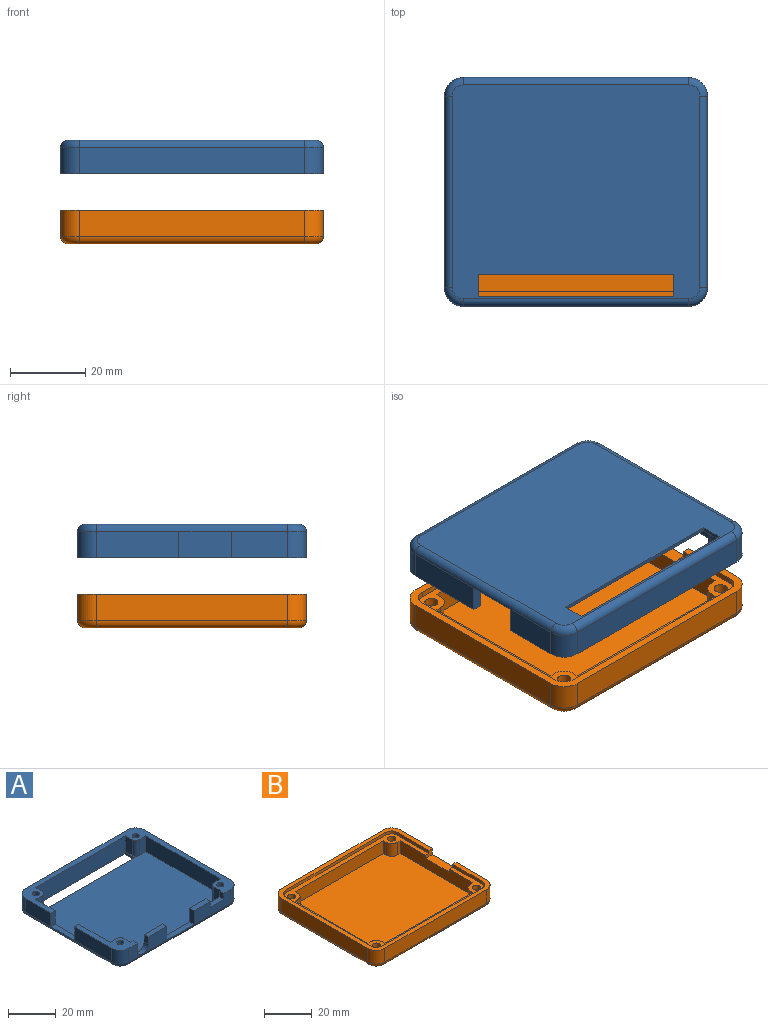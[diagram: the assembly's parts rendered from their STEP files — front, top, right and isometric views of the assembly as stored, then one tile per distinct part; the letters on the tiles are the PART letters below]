
ASSEMBLY  parts=2 mates=1
PART A: 64 faces, bbox 70.8x61.8x9 mm
  f0: plane 15x7mm, normal (-1,0,0), area 105mm2, adj f3,f29,f38,f49
  f1: plane 8.25x7mm, normal (0,-1,0), area 37.3mm2, adj f8,f30,f36,f45,f63
  f2: plane 14.25x7mm, normal (0,-1,0), area 79.3mm2, adj f6,f33,f37,f45,f63
  f3: plane 70x61mm, normal (0,0,1), area 449.4mm2, adj f0,f4,f7,f9,f11,f12,f14,f15
  f4: plane 53x8mm, normal (0,1,0), area 247mm2, adj f3,f5,f6,f8,f21,f22,f24,f33
  f5: plane 9.5x2.5mm, normal (0,0,1), area 23.7mm2, adj f4,f11,f34,f41
  f6: plane 11x2.5mm, normal (0,0,1), area 27.5mm2, adj f2,f4,f33,f37
  f7: plane 44x8mm, normal (1,0,0), area 254mm2, adj f3,f8,f14,f23,f24,f38,f39,f40
  f8: plane 27x10mm, normal (0,0,1), area 109mm2, adj f1,f4,f7,f10,f22,f23,f28,f30
  f9: plane 60x7mm, normal (0,1,0), area 420mm2, adj f3,f29,f32,f50
  f10: plane 22x7mm, normal (-1,0,0), area 154mm2, adj f8,f30,f39,f49
  f11: plane 21.5x7mm, normal (0,-1,0), area 126.5mm2, adj f3,f5,f31,f34,f41,f42,f43,f45
  f12: plane 51x7mm, normal (1,0,0), area 357mm2, adj f3,f31,f32,f46
  f13: plane 66x57mm, normal (0,0,-1), area 3442.3mm2, adj f16,f44,f45,f46,f47,f48,f49,f50
  f14: plane 8x4mm, normal (0,-1,0), area 32mm2, adj f3,f7,f24,f25
  f15: plane 8x4mm, normal (1,0,0), area 32mm2, adj f3,f16,f24,f25
  f16: plane 53x9mm, normal (0,-1,0), area 476mm2, adj f3,f13,f15,f17,f24,f52,f54
  f17: plane 8x4mm, normal (-1,0,0), area 32mm2, adj f3,f16,f24,f26
  f18: plane 8x4mm, normal (0,-1,0), area 32mm2, adj f3,f19,f24,f26
  f19: plane 44x8mm, normal (-1,0,0), area 352mm2, adj f3,f18,f20,f24
  f20: plane 8x4mm, normal (0,1,0), area 32mm2, adj f3,f19,f24,f27
  f21: plane 8x4mm, normal (-1,0,0), area 32mm2, adj f3,f4,f24,f27
  f22: plane 8x4mm, normal (1,0,0), area 32mm2, adj f4,f8,f24,f28
  f23: plane 8x4mm, normal (0,1,0), area 32mm2, adj f7,f8,f24,f28
  f24: plane 65x56mm, normal (0,0,1), area 3187.4mm2, adj f4,f7,f14,f15,f16,f17,f18,f19
  f25: cylinder r=2mm len=8mm, axis (0,0,-1), area 25.1mm2, adj f3,f14,f15,f24
  f26: cylinder r=2mm len=8mm, axis (0,0,-1), area 25.1mm2, adj f3,f17,f18,f24
  f27: cylinder r=2mm len=8mm, axis (0,0,-1), area 25.1mm2, adj f3,f20,f21,f24
  f28: cylinder r=2mm len=8mm, axis (0,0,-1), area 25.1mm2, adj f8,f22,f23,f24
  f29: cylinder r=5mm len=7mm, axis (0,0,1), area 55mm2, adj f0,f3,f9,f51
  f30: cylinder r=5mm len=7mm, axis (0,0,-1), area 55mm2, adj f1,f8,f10,f47
  f31: cylinder r=5mm len=7mm, axis (0,0,1), area 55mm2, adj f3,f11,f12,f44
  f32: cylinder r=5mm len=7mm, axis (0,0,-1), area 55mm2, adj f3,f9,f12,f48
  f33: plane 7x2.5mm, normal (1,0,0), area 17.5mm2, adj f2,f4,f6,f35
  f34: plane 7x2.5mm, normal (-1,0,0), area 17.5mm2, adj f4,f5,f11,f35
  f35: plane 16x2.5mm, normal (0,0,1), area 40mm2, adj f4,f33,f34,f45
  f36: plane 3.75x2.5mm, normal (1,0,0), area 9.4mm2, adj f1,f4,f8,f63
  f37: plane 3.75x2.5mm, normal (-1,0,0), area 9.4mm2, adj f2,f4,f6,f63
  f38: plane 7x2.5mm, normal (0,-1,0), area 17.5mm2, adj f0,f3,f7,f40
  f39: plane 7x2.5mm, normal (0,1,0), area 17.5mm2, adj f7,f8,f10,f40
  f40: plane 14x2.5mm, normal (0,0,1), area 35mm2, adj f7,f38,f39,f49
  f41: plane 3x2.5mm, normal (1,0,0), area 7.5mm2, adj f4,f5,f11,f43
  f42: plane 3x2.5mm, normal (-1,0,0), area 7.5mm2, adj f3,f4,f11,f43
  f43: plane 8x2.5mm, normal (0,0,1), area 20mm2, adj f4,f11,f41,f42
  f44: torus R=3mm, axis (0,0,1), area 21.1mm2, adj f13,f31,f45,f46
  f45: cylinder r=2mm len=60mm, axis (1,0,0), area 188.5mm2, adj f1,f2,f11,f13,f35,f44,f47
  f46: cylinder r=2mm len=51mm, axis (0,1,0), area 160.2mm2, adj f12,f13,f44,f48
  f47: torus R=3mm, axis (0,0,1), area 21.1mm2, adj f13,f30,f45,f49
  f48: torus R=3mm, axis (0,0,1), area 21.1mm2, adj f13,f32,f46,f50
  f49: cylinder r=2mm len=51mm, axis (0,-1,0), area 160.2mm2, adj f0,f10,f13,f40,f47,f51
  f50: cylinder r=2mm len=60mm, axis (-1,0,0), area 188.5mm2, adj f9,f13,f48,f51
  f51: torus R=3mm, axis (0,0,1), area 21.1mm2, adj f13,f29,f49,f50
  f52: plane 6x1mm, normal (1,0,0), area 6mm2, adj f13,f16,f24,f53
  f53: plane 52x1mm, normal (0,1,0), area 52mm2, adj f13,f24,f52,f54
  f54: plane 6x1mm, normal (-1,0,0), area 6mm2, adj f13,f16,f24,f53
  f55: cone r=0mm half-angle=59deg, axis (0,0,1), area 8.2mm2, adj f56
  f56: cylinder r=1.5mm len=7mm, axis (0,0,1), area 66mm2, adj f8,f55
  f57: cone r=0mm half-angle=59deg, axis (0,0,1), area 8.2mm2, adj f58
  f58: cylinder r=1.5mm len=7mm, axis (0,0,1), area 66mm2, adj f3,f57
  f59: cone r=0mm half-angle=59deg, axis (0,0,1), area 8.2mm2, adj f60
  f60: cylinder r=1.5mm len=7mm, axis (0,0,1), area 66mm2, adj f3,f59
  f61: cone r=0mm half-angle=59deg, axis (0,0,1), area 8.2mm2, adj f62
  f62: cylinder r=1.5mm len=7mm, axis (0,0,1), area 66mm2, adj f3,f61
  f63: cylinder r=3.25mm len=6.5mm, axis (0,1,0), area 25.5mm2, adj f1,f2,f4,f36,f37
PART B: 60 faces, bbox 70.8x61.8x9 mm
  f0: cylinder r=1.75mm len=5.1mm, axis (0,0,-1), area 56.1mm2, adj f8,f50
  f1: cylinder r=1.75mm len=5.1mm, axis (0,0,-1), area 56.1mm2, adj f8,f48
  f2: cylinder r=1.75mm len=5.1mm, axis (0,0,-1), area 56.1mm2, adj f8,f46
  f3: cylinder r=1.75mm len=5.1mm, axis (0,0,-1), area 56.1mm2, adj f8,f44
  f4: plane 18.5x1.5mm, normal (-1,0,0), area 27.8mm2, adj f5,f8,f29,f39
  f5: plane 70x61mm, normal (0,0,1), area 469.1mm2, adj f4,f6,f9,f10,f11,f12,f13,f14
  f6: plane 51x7mm, normal (1,0,0), area 315mm2, adj f5,f29,f30,f31,f42,f43,f56
  f7: plane 43x6.5mm, normal (-1,0,0), area 258.5mm2, adj f8,f22,f23,f28,f29,f30,f31
  f8: plane 66x57mm, normal (0,0,1), area 488.5mm2, adj f0,f1,f2,f3,f4,f7,f9,f10
  f9: plane 59x1.5mm, normal (0,-1,0), area 88.5mm2, adj f5,f8,f36,f39
  f10: plane 50x1.5mm, normal (1,0,0), area 75mm2, adj f5,f8,f36,f37
  f11: plane 59x1.5mm, normal (0,1,0), area 88.5mm2, adj f5,f8,f37,f38
  f12: plane 17.5x1.5mm, normal (-1,0,0), area 26.3mm2, adj f5,f8,f30,f38
  f13: plane 60x7mm, normal (0,1,0), area 420mm2, adj f5,f40,f43,f59
  f14: plane 51x7mm, normal (-1,0,0), area 357mm2, adj f5,f40,f41,f55
  f15: plane 60x7mm, normal (0,-1,0), area 420mm2, adj f5,f41,f42,f52
  f16: plane 66x57mm, normal (0,0,-1), area 3621.5mm2, adj f45,f47,f49,f51,f52,f53,f54,f55
  f17: plane 43x6.5mm, normal (1,0,0), area 279.5mm2, adj f8,f18,f27,f28
  f18: plane 6.5x1.5mm, normal (0,-1,0), area 9.8mm2, adj f8,f17,f28,f32
  f19: plane 6.5x1.5mm, normal (1,0,0), area 9.7mm2, adj f8,f20,f28,f32
  f20: plane 52x6.5mm, normal (0,-1,0), area 338mm2, adj f8,f19,f21,f28
  f21: plane 6.5x1.5mm, normal (-1,0,0), area 9.7mm2, adj f8,f20,f28,f33
  f22: plane 6.5x1.5mm, normal (0,-1,0), area 9.8mm2, adj f7,f8,f28,f33
  f23: plane 6.5x1.5mm, normal (0,1,0), area 9.8mm2, adj f7,f8,f28,f34
  f24: plane 6.5x1.5mm, normal (-1,0,0), area 9.7mm2, adj f8,f25,f28,f34
  f25: plane 52x6.5mm, normal (0,1,0), area 338mm2, adj f8,f24,f26,f28
  f26: plane 6.5x1.5mm, normal (1,0,0), area 9.7mm2, adj f8,f25,f28,f35
  f27: plane 6.5x1.5mm, normal (0,1,0), area 9.8mm2, adj f8,f17,f28,f35
  f28: plane 62x53mm, normal (0,0,1), area 3196.5mm2, adj f7,f17,f18,f19,f20,f21,f22,f23
  f29: plane 4x3mm, normal (0,-1,0), area 9mm2, adj f4,f5,f6,f7,f8,f31
  f30: plane 4x3mm, normal (0,1,0), area 9mm2, adj f5,f6,f7,f8,f12,f31
  f31: plane 14x4mm, normal (0,0,1), area 56mm2, adj f6,f7,f29,f30
  f32: cylinder r=3.5mm len=6.5mm, axis (0,0,-1), area 35.7mm2, adj f8,f18,f19,f28
  f33: cylinder r=3.5mm len=6.5mm, axis (0,0,-1), area 35.7mm2, adj f8,f21,f22,f28
  f34: cylinder r=3.5mm len=6.5mm, axis (0,0,-1), area 35.7mm2, adj f8,f23,f24,f28
  f35: cylinder r=3.5mm len=6.5mm, axis (0,0,-1), area 35.7mm2, adj f8,f26,f27,f28
  f36: cylinder r=3.5mm len=3.5mm, axis (0,0,1), area 8.2mm2, adj f5,f8,f9,f10
  f37: cylinder r=3.5mm len=3.5mm, axis (0,0,-1), area 8.2mm2, adj f5,f8,f10,f11
  f38: cylinder r=3.5mm len=3.5mm, axis (0,0,1), area 8.2mm2, adj f5,f8,f11,f12
  f39: cylinder r=3.5mm len=3.5mm, axis (0,0,-1), area 8.2mm2, adj f4,f5,f8,f9
  f40: cylinder r=5mm len=7mm, axis (0,0,1), area 55mm2, adj f5,f13,f14,f57
  f41: cylinder r=5mm len=7mm, axis (0,0,-1), area 55mm2, adj f5,f14,f15,f53
  f42: cylinder r=5mm len=7mm, axis (0,0,1), area 55mm2, adj f5,f6,f15,f54
  f43: cylinder r=5mm len=7mm, axis (0,0,-1), area 55mm2, adj f5,f6,f13,f58
  f44: cone r=0mm half-angle=59deg, axis (0,0,-1), area 27.5mm2, adj f3,f45
  f45: cylinder r=3.25mm len=6.5mm, axis (0,0,-1), area 30.6mm2, adj f16,f44
  f46: cone r=0mm half-angle=59deg, axis (0,0,-1), area 27.5mm2, adj f2,f47
  f47: cylinder r=3.25mm len=6.5mm, axis (0,0,-1), area 30.6mm2, adj f16,f46
  f48: cone r=0mm half-angle=59deg, axis (0,0,-1), area 27.5mm2, adj f1,f49
  f49: cylinder r=3.25mm len=6.5mm, axis (0,0,-1), area 30.6mm2, adj f16,f48
  f50: cone r=0mm half-angle=59deg, axis (0,0,-1), area 27.5mm2, adj f0,f51
  f51: cylinder r=3.25mm len=6.5mm, axis (0,0,-1), area 30.6mm2, adj f16,f50
  f52: cylinder r=2mm len=60mm, axis (1,0,0), area 188.5mm2, adj f15,f16,f53,f54
  f53: torus R=3mm, axis (0,0,1), area 21.1mm2, adj f16,f41,f52,f55
  f54: torus R=3mm, axis (0,0,1), area 21.1mm2, adj f16,f42,f52,f56
  f55: cylinder r=2mm len=51mm, axis (0,-1,0), area 160.2mm2, adj f14,f16,f53,f57
  f56: cylinder r=2mm len=51mm, axis (0,1,0), area 160.2mm2, adj f6,f16,f54,f58
  f57: torus R=3mm, axis (0,0,1), area 21.1mm2, adj f16,f40,f55,f59
  f58: torus R=3mm, axis (0,0,1), area 21.1mm2, adj f16,f43,f56,f59
  f59: cylinder r=2mm len=60mm, axis (-1,0,0), area 188.5mm2, adj f13,f16,f57,f58
PLACE A rot(axis=(1,0,0),180deg) t=(0,0,27.63)mm
PLACE B at identity
MATE slider A.f59 <-> B.f3  axis (0,0,-1) through (29.5,-25,26.53)mm
